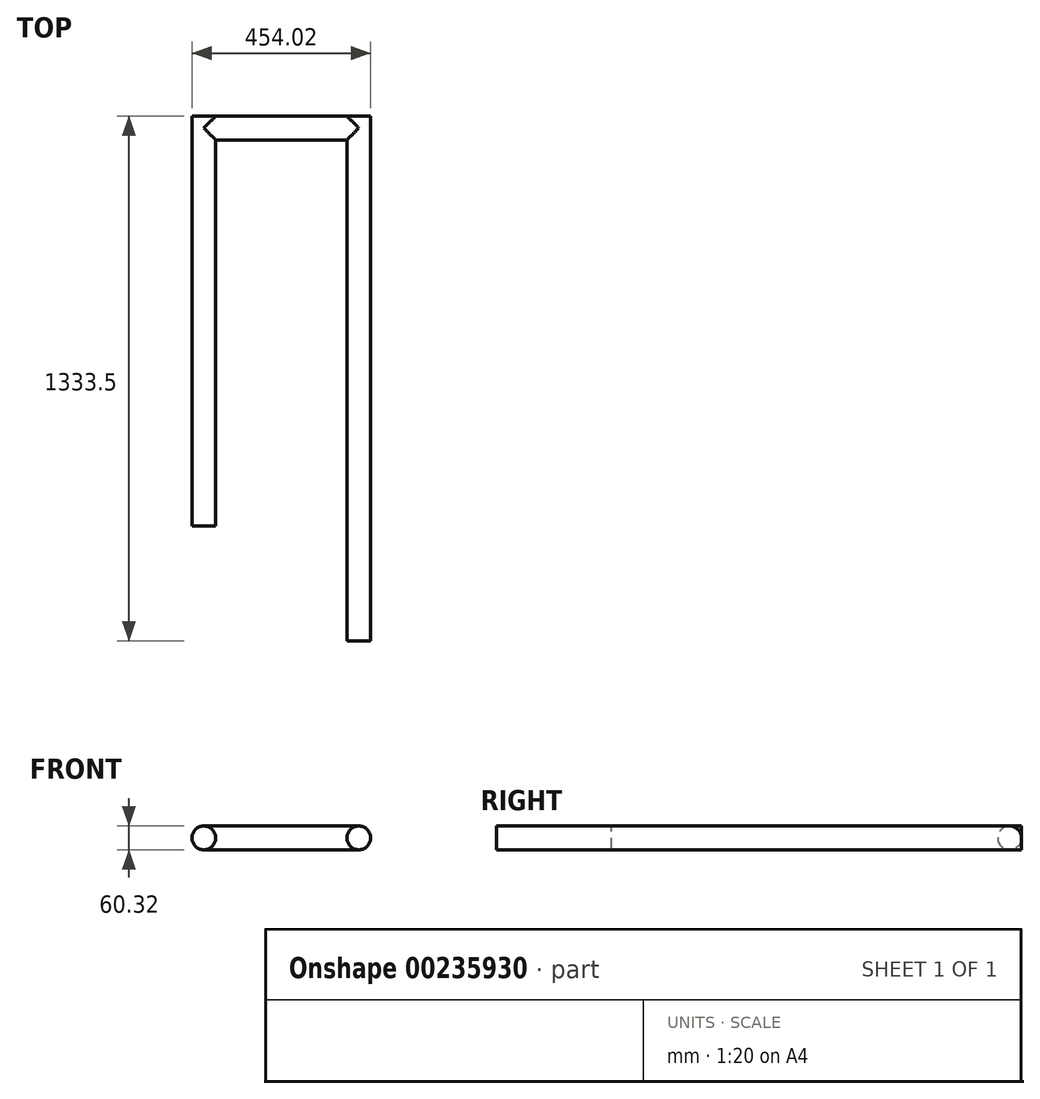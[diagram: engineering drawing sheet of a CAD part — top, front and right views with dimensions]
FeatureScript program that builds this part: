
annotation { "Feature Type Name" : "Feature", "Feature Type Description" : "" }
export const myFeature = defineFeature(function(context is Context, id is Id, definition is map)
    precondition{}
    {
        {
            var Q0;
            Q0=qCreatedBy(makeId("Front.planeOp"),FACE);
            var sketch = newSketch(context, id + "F0", { "sketchPlane" : qUnion([Q0])});
            skCircle(sketch, "E0", {"center": v(0, 0) * mm, "radius": 30.16 * mm});
            skSolve(sketch);
        }
        {
            var Q0;
            Q0 = qSketchRegion(id + "F0", true);
            extrude(context, id + "F1", {"entities" : qUnion([Q0]), "depth" : 1041.4 * mm});
        }
        {
            var Q0;
            Q0=qCreatedBy(makeId("Right.planeOp"),FACE);
            var sketch = newSketch(context, id + "F2", { "sketchPlane" : qUnion([Q0])});
            skCircle(sketch, "E1", {"center": v(-30.16, 0) * mm, "radius": 30.16 * mm});
            skSolve(sketch);
        }
        {
            var Q0;
            Q0 = qSketchRegion(id + "F2", true);
            extrude(context, id + "F3", {"entities" : qUnion([Q0]), "operationType" : NewBodyOperationType.ADD, "depth" : 393.7 * mm});
        }
        {
            var Q0;
            Q0=qCreatedBy(makeId("Front.planeOp"),FACE);
            var sketch = newSketch(context, id + "F4", { "sketchPlane" : qUnion([Q0])});
            skPoint(sketch, "E2", {"position": v(393.7, 0) * mm});
            skCircle(sketch, "E3", {"center": v(393.7, 0) * mm, "radius": 30.16 * mm});
            skSolve(sketch);
        }
        {
            var Q0;
            Q0=makeQuery(id+"F4.imprint","IMPRINT",FACE,{"disambiguationData":[TD([[makeQuery(id+"F4.imprint","IMPRINT",EDGE,{"derivedFrom":sQuery(id+"F4.wireOp",EDGE,"E3")}),1.0]])]});
            extrude(context, id + "F5", {"entities" : qUnion([Q0]), "operationType" : NewBodyOperationType.ADD, "depth" : 1333.5 * mm});
        }
    });
